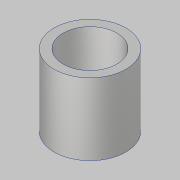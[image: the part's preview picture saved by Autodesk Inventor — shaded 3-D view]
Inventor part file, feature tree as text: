
AUTODESK INVENTOR PART (.ipt)
format: ipt  version: 2019.2 (Build 232265000, 265)  size: 86,528 bytes
history: native  units: mm
features: extrude x1, sketch x1
ambient origin geometry x8: Origin, YZ Plane, XZ Plane, XY Plane, X Axis, Y Axis, Z Axis, Center Point
bodies: Volumenkörper1 (feature_tree)
feature tree (2):
  extrude  "Extrusion1"  Depth=4.0mm
  sketch  "Skizze1"  dims[d1=0.5mm d2=4.0mm d3=4.0mm d4=0.0mm]
